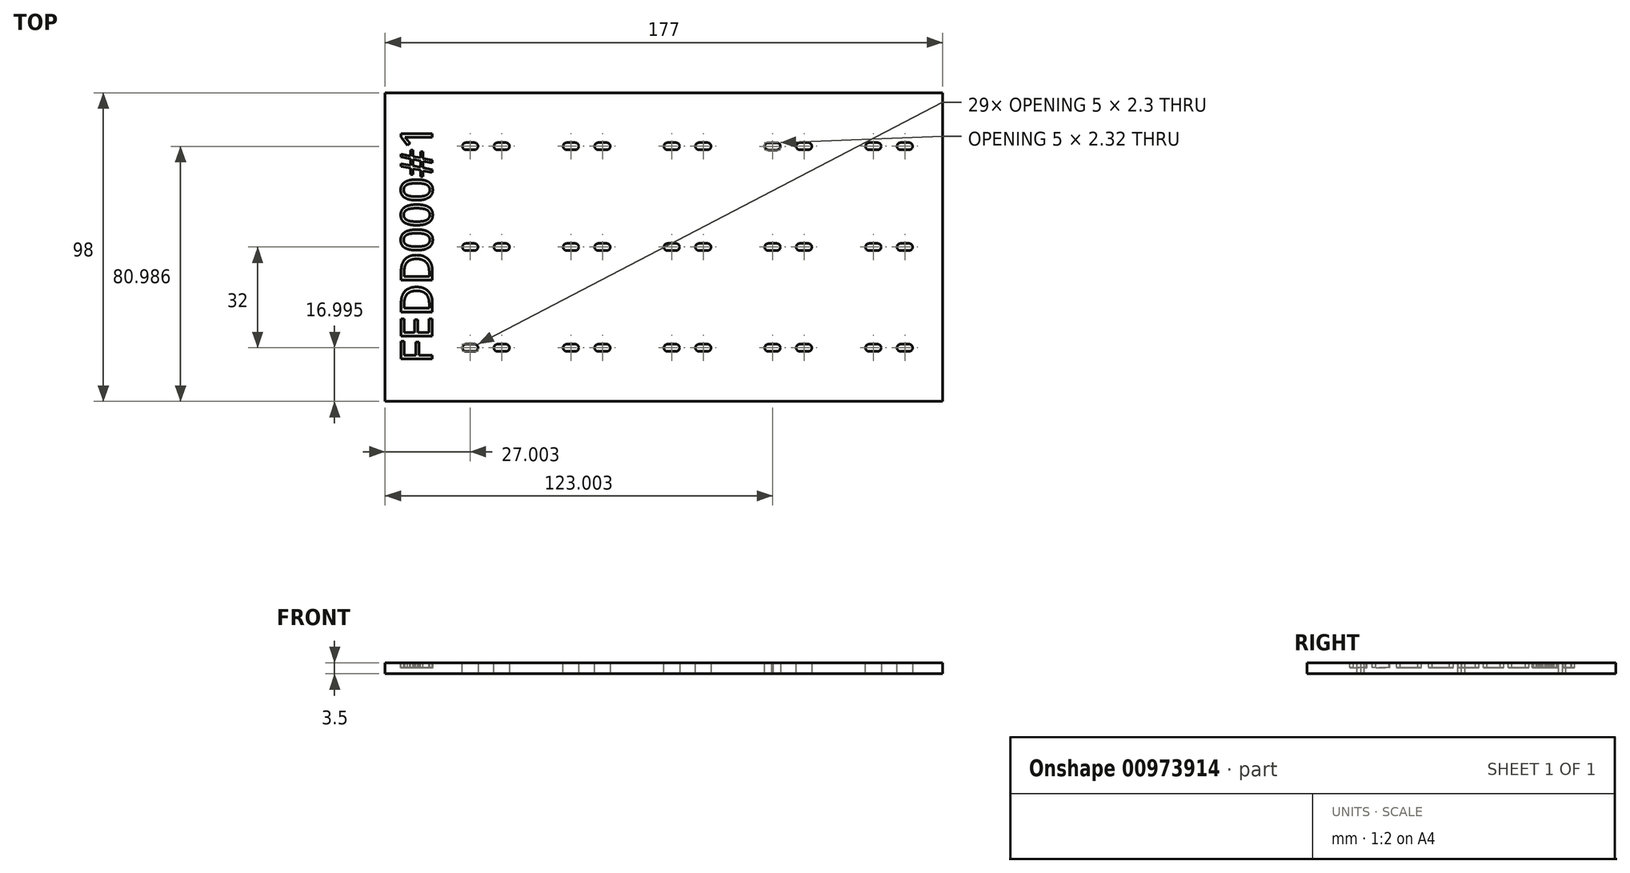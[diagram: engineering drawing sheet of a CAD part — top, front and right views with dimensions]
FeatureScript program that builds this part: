
annotation { "Feature Type Name" : "Feature", "Feature Type Description" : "" }
export const myFeature = defineFeature(function(context is Context, id is Id, definition is map)
    precondition{}
    {
        {
            var Q0;
            Q0=qCreatedBy(makeId("Top.planeOp"),FACE);
            var sketch = newSketch(context, id + "F0", { "sketchPlane" : qUnion([Q0])});
            skLineSegment(sketch, "E0.bottom", {"start": v(-87.55, 48.72) * mm, "end": v(89.45, 48.72) * mm});
            skLineSegment(sketch, "E0.top", {"start": v(-87.55, -49.28) * mm, "end": v(89.45, -49.28) * mm});
            skLineSegment(sketch, "E0.left", {"start": v(-87.55, 48.72) * mm, "end": v(-87.55, -49.28) * mm});
            skLineSegment(sketch, "E0.right", {"start": v(89.45, 48.72) * mm, "end": v(89.45, -49.28) * mm});
            skSolve(sketch);
        }
        {
            var Q0;
            Q0=makeQuery(id+"F0.imprint","IMPRINT",FACE,{"disambiguationData":[TD([[makeQuery(id+"F0.imprint","IMPRINT",EDGE,{"derivedFrom":sQuery(id+"F0.wireOp",EDGE,"E0.bottom")}),-1.0]])]});
            extrude(context, id + "F1", {"entities" : qUnion([Q0]), "depth" : 3.5 * mm, "offsetDistance" : 25 * mm});
        }
        {
            var Q0;
            Q0=makeQuery(id+"F1.opExtrude","CAP_FACE",FACE,{"disambiguationData":[OSD([sQuery(id+"F0.wireOp",EDGE,"E0.bottom"),sQuery(id+"F0.wireOp",EDGE,"E0.top"),sQuery(id+"F0.wireOp",EDGE,"E0.left"),sQuery(id+"F0.wireOp",EDGE,"E0.right")])],"isStart":false});
            var sketch = newSketch(context, id + "F2", { "sketchPlane" : qUnion([Q0])});
            skText(sketch, "E1", { "text": "FEDD000#1", "fontName": "OpenSans-Regular.ttf"});
            const initialGuessF2  = {"E1": [-0.07255, -0.03713, 0, 1, 0.01]};
            skSetInitialGuess(sketch, initialGuessF2);
            skSolve(sketch);
        }
        {
            var Q0;
            Q0=qSketchRegion(id+"F2",true);
            extrude(context, id + "F3", {"entities" : qUnion([Q0]), "operationType" : NewBodyOperationType.REMOVE, "oppositeDirection" : true, "depth" : 1.5 * mm, "offsetDistance" : 25 * mm});
        }
        {
            var Q0;
            {var subQ0=sQuery(id+"F0.wireOp",EDGE,"E0.left");var subQ1=sQuery(id+"F0.wireOp",EDGE,"E0.bottom");var subQ2=sQuery(id+"F0.wireOp",EDGE,"E0.right");var subQ3=sQuery(id+"F0.wireOp",EDGE,"E0.top");Q0=makeQuery(id+"F3.boolean.opBoolean","SPLIT",FACE,{"disambiguationData":[TD([makeQuery(id+"F1.opExtrude","SWEPT_FACE",FACE,{"disambiguationData":[OSD([subQ1])]})])],"derivedFrom":makeQuery(id+"F1.opExtrude","CAP_FACE",FACE,{"disambiguationData":[OSD([subQ1,subQ3,subQ0,subQ2])],"isStart":false})});}
            var sketch = newSketch(context, id + "F4", { "sketchPlane" : qUnion([Q0])});
            skCircle(sketch, "E2", {"center": v(-60.55, 31.72) * mm, "radius": 1.15 * mm});
            skCircle(sketch, "E3", {"center": v(-50.55, 31.72) * mm, "radius": 1.15 * mm});
            skCircle(sketch, "E4", {"center": v(-28.55, 31.72) * mm, "radius": 1.15 * mm});
            skCircle(sketch, "E5", {"center": v(-18.55, 31.72) * mm, "radius": 1.15 * mm});
            skCircle(sketch, "E6", {"center": v(3.45, 31.72) * mm, "radius": 1.15 * mm});
            skCircle(sketch, "E7", {"center": v(13.45, 31.72) * mm, "radius": 1.15 * mm});
            skCircle(sketch, "E8", {"center": v(35.45, 31.72) * mm, "radius": 1.15 * mm});
            skCircle(sketch, "E9", {"center": v(45.45, 31.72) * mm, "radius": 1.15 * mm});
            skCircle(sketch, "E10", {"center": v(67.45, 31.72) * mm, "radius": 1.15 * mm});
            skCircle(sketch, "E11", {"center": v(77.45, 31.72) * mm, "radius": 1.15 * mm});
            skCircle(sketch, "E12", {"center": v(-60.55, -0.28) * mm, "radius": 1.15 * mm});
            skCircle(sketch, "E13", {"center": v(-50.55, -0.28) * mm, "radius": 1.15 * mm});
            skCircle(sketch, "E14", {"center": v(-28.55, -0.28) * mm, "radius": 1.15 * mm});
            skCircle(sketch, "E15", {"center": v(-18.55, -0.28) * mm, "radius": 1.15 * mm});
            skCircle(sketch, "E16", {"center": v(3.45, -0.28) * mm, "radius": 1.15 * mm});
            skCircle(sketch, "E17", {"center": v(13.45, -0.28) * mm, "radius": 1.15 * mm});
            skCircle(sketch, "E18", {"center": v(35.45, -0.28) * mm, "radius": 1.15 * mm});
            skCircle(sketch, "E19", {"center": v(45.45, -0.28) * mm, "radius": 1.15 * mm});
            skCircle(sketch, "E20", {"center": v(67.45, -0.28) * mm, "radius": 1.15 * mm});
            skCircle(sketch, "E21", {"center": v(77.45, -0.28) * mm, "radius": 1.15 * mm});
            skCircle(sketch, "E22", {"center": v(-60.55, -32.28) * mm, "radius": 1.15 * mm});
            skCircle(sketch, "E23", {"center": v(-50.55, -32.28) * mm, "radius": 1.15 * mm});
            skCircle(sketch, "E24", {"center": v(-28.55, -32.28) * mm, "radius": 1.15 * mm});
            skCircle(sketch, "E25", {"center": v(-18.55, -32.28) * mm, "radius": 1.15 * mm});
            skCircle(sketch, "E26", {"center": v(3.45, -32.28) * mm, "radius": 1.15 * mm});
            skCircle(sketch, "E27", {"center": v(13.45, -32.28) * mm, "radius": 1.15 * mm});
            skCircle(sketch, "E28", {"center": v(35.45, -32.28) * mm, "radius": 1.15 * mm});
            skCircle(sketch, "E29", {"center": v(45.45, -32.28) * mm, "radius": 1.15 * mm});
            skCircle(sketch, "E30", {"center": v(67.45, -32.28) * mm, "radius": 1.15 * mm});
            skCircle(sketch, "E31", {"center": v(77.45, -32.28) * mm, "radius": 1.15 * mm});
            skLineSegment(sketch, "E32.bottom", {"start": v(-53.05, 32.87) * mm, "end": v(-48.05, 32.87) * mm});
            skLineSegment(sketch, "E32.top", {"start": v(-53.05, 30.57) * mm, "end": v(-48.05, 30.57) * mm});
            skLineSegment(sketch, "E32.left", {"start": v(-53.05, 32.87) * mm, "end": v(-53.05, 30.57) * mm});
            skLineSegment(sketch, "E32.right", {"start": v(-48.05, 32.87) * mm, "end": v(-48.05, 30.57) * mm});
            skLineSegment(sketch, "E33.bottom", {"start": v(-63.05, 32.87) * mm, "end": v(-58.05, 32.87) * mm});
            skLineSegment(sketch, "E33.top", {"start": v(-63.05, 30.57) * mm, "end": v(-58.05, 30.57) * mm});
            skLineSegment(sketch, "E33.left", {"start": v(-63.05, 32.87) * mm, "end": v(-63.05, 30.57) * mm});
            skLineSegment(sketch, "E33.right", {"start": v(-58.05, 32.87) * mm, "end": v(-58.05, 30.57) * mm});
            skLineSegment(sketch, "E34.bottom", {"start": v(-31.05, 32.87) * mm, "end": v(-26.05, 32.87) * mm});
            skLineSegment(sketch, "E34.top", {"start": v(-31.05, 30.57) * mm, "end": v(-26.05, 30.57) * mm});
            skLineSegment(sketch, "E34.left", {"start": v(-31.05, 32.87) * mm, "end": v(-31.05, 30.57) * mm});
            skLineSegment(sketch, "E34.right", {"start": v(-26.05, 32.87) * mm, "end": v(-26.05, 30.57) * mm});
            skLineSegment(sketch, "E35.bottom", {"start": v(-21.05, 32.87) * mm, "end": v(-16.05, 32.87) * mm});
            skLineSegment(sketch, "E35.top", {"start": v(-21.05, 30.57) * mm, "end": v(-16.05, 30.57) * mm});
            skLineSegment(sketch, "E35.left", {"start": v(-21.05, 32.87) * mm, "end": v(-21.05, 30.57) * mm});
            skLineSegment(sketch, "E35.right", {"start": v(-16.05, 32.87) * mm, "end": v(-16.05, 30.57) * mm});
            skLineSegment(sketch, "E36.bottom", {"start": v(0.95, 32.87) * mm, "end": v(5.95, 32.87) * mm});
            skLineSegment(sketch, "E36.top", {"start": v(0.95, 30.57) * mm, "end": v(5.95, 30.57) * mm});
            skLineSegment(sketch, "E36.left", {"start": v(0.95, 32.87) * mm, "end": v(0.95, 30.57) * mm});
            skLineSegment(sketch, "E36.right", {"start": v(5.95, 32.87) * mm, "end": v(5.95, 30.57) * mm});
            skLineSegment(sketch, "E37.bottom", {"start": v(10.95, 32.87) * mm, "end": v(15.95, 32.87) * mm});
            skLineSegment(sketch, "E37.top", {"start": v(10.95, 30.57) * mm, "end": v(15.95, 30.57) * mm});
            skLineSegment(sketch, "E37.left", {"start": v(10.95, 32.87) * mm, "end": v(10.95, 30.57) * mm});
            skLineSegment(sketch, "E37.right", {"start": v(15.95, 32.87) * mm, "end": v(15.95, 30.57) * mm});
            skLineSegment(sketch, "E38.bottom", {"start": v(32.95, 32.85) * mm, "end": v(37.95, 32.85) * mm});
            skLineSegment(sketch, "E38.top", {"start": v(32.95, 30.55) * mm, "end": v(37.95, 30.55) * mm});
            skLineSegment(sketch, "E38.left", {"start": v(32.95, 32.85) * mm, "end": v(32.95, 30.55) * mm});
            skLineSegment(sketch, "E38.right", {"start": v(37.95, 32.85) * mm, "end": v(37.95, 30.55) * mm});
            skLineSegment(sketch, "E39.bottom", {"start": v(42.95, 32.87) * mm, "end": v(47.95, 32.87) * mm});
            skLineSegment(sketch, "E39.top", {"start": v(42.95, 30.57) * mm, "end": v(47.95, 30.57) * mm});
            skLineSegment(sketch, "E39.left", {"start": v(42.95, 32.87) * mm, "end": v(42.95, 30.57) * mm});
            skLineSegment(sketch, "E39.right", {"start": v(47.95, 32.87) * mm, "end": v(47.95, 30.57) * mm});
            skLineSegment(sketch, "E40.bottom", {"start": v(64.95, 32.87) * mm, "end": v(69.95, 32.87) * mm});
            skLineSegment(sketch, "E40.top", {"start": v(64.95, 30.57) * mm, "end": v(69.95, 30.57) * mm});
            skLineSegment(sketch, "E40.left", {"start": v(64.95, 32.87) * mm, "end": v(64.95, 30.57) * mm});
            skLineSegment(sketch, "E40.right", {"start": v(69.95, 32.87) * mm, "end": v(69.95, 30.57) * mm});
            skLineSegment(sketch, "E41.bottom", {"start": v(74.95, 32.87) * mm, "end": v(79.95, 32.87) * mm});
            skLineSegment(sketch, "E41.top", {"start": v(74.95, 30.57) * mm, "end": v(79.95, 30.57) * mm});
            skLineSegment(sketch, "E41.left", {"start": v(74.95, 32.87) * mm, "end": v(74.95, 30.57) * mm});
            skLineSegment(sketch, "E41.right", {"start": v(79.95, 32.87) * mm, "end": v(79.95, 30.57) * mm});
            skLineSegment(sketch, "E42.bottom", {"start": v(74.95, 0.87) * mm, "end": v(79.95, 0.87) * mm});
            skLineSegment(sketch, "E42.top", {"start": v(74.95, -1.43) * mm, "end": v(79.95, -1.43) * mm});
            skLineSegment(sketch, "E42.left", {"start": v(74.95, 0.87) * mm, "end": v(74.95, -1.43) * mm});
            skLineSegment(sketch, "E42.right", {"start": v(79.95, 0.87) * mm, "end": v(79.95, -1.43) * mm});
            skLineSegment(sketch, "E43.bottom", {"start": v(64.95, 0.87) * mm, "end": v(69.95, 0.87) * mm});
            skLineSegment(sketch, "E43.top", {"start": v(64.95, -1.43) * mm, "end": v(69.95, -1.43) * mm});
            skLineSegment(sketch, "E43.left", {"start": v(64.95, 0.87) * mm, "end": v(64.95, -1.43) * mm});
            skLineSegment(sketch, "E43.right", {"start": v(69.95, 0.87) * mm, "end": v(69.95, -1.43) * mm});
            skLineSegment(sketch, "E44.bottom", {"start": v(42.95, 0.87) * mm, "end": v(47.95, 0.87) * mm});
            skLineSegment(sketch, "E44.top", {"start": v(42.95, -1.43) * mm, "end": v(47.95, -1.43) * mm});
            skLineSegment(sketch, "E44.left", {"start": v(42.95, 0.87) * mm, "end": v(42.95, -1.43) * mm});
            skLineSegment(sketch, "E44.right", {"start": v(47.95, 0.87) * mm, "end": v(47.95, -1.43) * mm});
            skLineSegment(sketch, "E45.bottom", {"start": v(32.95, 0.87) * mm, "end": v(37.95, 0.87) * mm});
            skLineSegment(sketch, "E45.top", {"start": v(32.95, -1.43) * mm, "end": v(37.95, -1.43) * mm});
            skLineSegment(sketch, "E45.left", {"start": v(32.95, 0.87) * mm, "end": v(32.95, -1.43) * mm});
            skLineSegment(sketch, "E45.right", {"start": v(37.95, 0.87) * mm, "end": v(37.95, -1.43) * mm});
            skLineSegment(sketch, "E46.bottom", {"start": v(10.95, 0.87) * mm, "end": v(15.95, 0.87) * mm});
            skLineSegment(sketch, "E46.top", {"start": v(10.95, -1.43) * mm, "end": v(15.95, -1.43) * mm});
            skLineSegment(sketch, "E46.left", {"start": v(10.95, 0.87) * mm, "end": v(10.95, -1.43) * mm});
            skLineSegment(sketch, "E46.right", {"start": v(15.95, 0.87) * mm, "end": v(15.95, -1.43) * mm});
            skLineSegment(sketch, "E47.bottom", {"start": v(-63.05, 0.87) * mm, "end": v(-58.05, 0.87) * mm});
            skLineSegment(sketch, "E47.top", {"start": v(-63.05, -1.43) * mm, "end": v(-58.05, -1.43) * mm});
            skLineSegment(sketch, "E47.left", {"start": v(-63.05, 0.87) * mm, "end": v(-63.05, -1.43) * mm});
            skLineSegment(sketch, "E47.right", {"start": v(-58.05, 0.87) * mm, "end": v(-58.05, -1.43) * mm});
            skLineSegment(sketch, "E48.bottom", {"start": v(-53.05, 0.87) * mm, "end": v(-48.05, 0.87) * mm});
            skLineSegment(sketch, "E48.top", {"start": v(-53.05, -1.43) * mm, "end": v(-48.05, -1.43) * mm});
            skLineSegment(sketch, "E48.left", {"start": v(-53.05, 0.87) * mm, "end": v(-53.05, -1.43) * mm});
            skLineSegment(sketch, "E48.right", {"start": v(-48.05, 0.87) * mm, "end": v(-48.05, -1.43) * mm});
            skLineSegment(sketch, "E49.bottom", {"start": v(-31.05, 0.87) * mm, "end": v(-26.05, 0.87) * mm});
            skLineSegment(sketch, "E49.top", {"start": v(-31.05, -1.43) * mm, "end": v(-26.05, -1.43) * mm});
            skLineSegment(sketch, "E49.left", {"start": v(-31.05, 0.87) * mm, "end": v(-31.05, -1.43) * mm});
            skLineSegment(sketch, "E49.right", {"start": v(-26.05, 0.87) * mm, "end": v(-26.05, -1.43) * mm});
            skLineSegment(sketch, "E50.bottom", {"start": v(-21.05, 0.87) * mm, "end": v(-16.05, 0.87) * mm});
            skLineSegment(sketch, "E50.top", {"start": v(-21.05, -1.43) * mm, "end": v(-16.05, -1.43) * mm});
            skLineSegment(sketch, "E50.left", {"start": v(-21.05, 0.87) * mm, "end": v(-21.05, -1.43) * mm});
            skLineSegment(sketch, "E50.right", {"start": v(-16.05, 0.87) * mm, "end": v(-16.05, -1.43) * mm});
            skLineSegment(sketch, "E51.bottom", {"start": v(0.95, 0.87) * mm, "end": v(5.95, 0.87) * mm});
            skLineSegment(sketch, "E51.top", {"start": v(0.95, -1.43) * mm, "end": v(5.95, -1.43) * mm});
            skLineSegment(sketch, "E51.left", {"start": v(0.95, 0.87) * mm, "end": v(0.95, -1.43) * mm});
            skLineSegment(sketch, "E51.right", {"start": v(5.95, 0.87) * mm, "end": v(5.95, -1.43) * mm});
            skLineSegment(sketch, "E52.bottom", {"start": v(-63.05, -31.13) * mm, "end": v(-58.05, -31.13) * mm});
            skLineSegment(sketch, "E52.top", {"start": v(-63.05, -33.43) * mm, "end": v(-58.05, -33.43) * mm});
            skLineSegment(sketch, "E52.left", {"start": v(-63.05, -31.13) * mm, "end": v(-63.05, -33.43) * mm});
            skLineSegment(sketch, "E52.right", {"start": v(-58.05, -31.13) * mm, "end": v(-58.05, -33.43) * mm});
            skLineSegment(sketch, "E53.bottom", {"start": v(-53.05, -31.13) * mm, "end": v(-48.05, -31.13) * mm});
            skLineSegment(sketch, "E53.top", {"start": v(-53.05, -33.43) * mm, "end": v(-48.05, -33.43) * mm});
            skLineSegment(sketch, "E53.left", {"start": v(-53.05, -31.13) * mm, "end": v(-53.05, -33.43) * mm});
            skLineSegment(sketch, "E53.right", {"start": v(-48.05, -31.13) * mm, "end": v(-48.05, -33.43) * mm});
            skLineSegment(sketch, "E54.bottom", {"start": v(-31.05, -31.13) * mm, "end": v(-26.05, -31.13) * mm});
            skLineSegment(sketch, "E54.top", {"start": v(-31.05, -33.43) * mm, "end": v(-26.05, -33.43) * mm});
            skLineSegment(sketch, "E54.left", {"start": v(-31.05, -31.13) * mm, "end": v(-31.05, -33.43) * mm});
            skLineSegment(sketch, "E54.right", {"start": v(-26.05, -31.13) * mm, "end": v(-26.05, -33.43) * mm});
            skLineSegment(sketch, "E55.bottom", {"start": v(-21.05, -31.13) * mm, "end": v(-16.05, -31.13) * mm});
            skLineSegment(sketch, "E55.top", {"start": v(-21.05, -33.43) * mm, "end": v(-16.05, -33.43) * mm});
            skLineSegment(sketch, "E55.left", {"start": v(-21.05, -31.13) * mm, "end": v(-21.05, -33.43) * mm});
            skLineSegment(sketch, "E55.right", {"start": v(-16.05, -31.13) * mm, "end": v(-16.05, -33.43) * mm});
            skLineSegment(sketch, "E56.bottom", {"start": v(0.95, -31.13) * mm, "end": v(5.95, -31.13) * mm});
            skLineSegment(sketch, "E56.top", {"start": v(0.95, -33.43) * mm, "end": v(5.95, -33.43) * mm});
            skLineSegment(sketch, "E56.left", {"start": v(0.95, -31.13) * mm, "end": v(0.95, -33.43) * mm});
            skLineSegment(sketch, "E56.right", {"start": v(5.95, -31.13) * mm, "end": v(5.95, -33.43) * mm});
            skLineSegment(sketch, "E57.bottom", {"start": v(10.95, -31.13) * mm, "end": v(15.95, -31.13) * mm});
            skLineSegment(sketch, "E57.top", {"start": v(10.95, -33.43) * mm, "end": v(15.95, -33.43) * mm});
            skLineSegment(sketch, "E57.left", {"start": v(10.95, -31.13) * mm, "end": v(10.95, -33.43) * mm});
            skLineSegment(sketch, "E57.right", {"start": v(15.95, -31.13) * mm, "end": v(15.95, -33.43) * mm});
            skLineSegment(sketch, "E58.bottom", {"start": v(32.95, -31.13) * mm, "end": v(37.95, -31.13) * mm});
            skLineSegment(sketch, "E58.top", {"start": v(32.95, -33.43) * mm, "end": v(37.95, -33.43) * mm});
            skLineSegment(sketch, "E58.left", {"start": v(32.95, -31.13) * mm, "end": v(32.95, -33.43) * mm});
            skLineSegment(sketch, "E58.right", {"start": v(37.95, -31.13) * mm, "end": v(37.95, -33.43) * mm});
            skLineSegment(sketch, "E59.bottom", {"start": v(42.95, -31.13) * mm, "end": v(47.95, -31.13) * mm});
            skLineSegment(sketch, "E59.top", {"start": v(42.95, -33.43) * mm, "end": v(47.95, -33.43) * mm});
            skLineSegment(sketch, "E59.left", {"start": v(42.95, -31.13) * mm, "end": v(42.95, -33.43) * mm});
            skLineSegment(sketch, "E59.right", {"start": v(47.95, -31.13) * mm, "end": v(47.95, -33.43) * mm});
            skLineSegment(sketch, "E60.bottom", {"start": v(64.95, -31.13) * mm, "end": v(69.95, -31.13) * mm});
            skLineSegment(sketch, "E60.top", {"start": v(64.95, -33.43) * mm, "end": v(69.95, -33.43) * mm});
            skLineSegment(sketch, "E60.left", {"start": v(64.95, -31.13) * mm, "end": v(64.95, -33.43) * mm});
            skLineSegment(sketch, "E60.right", {"start": v(69.95, -31.13) * mm, "end": v(69.95, -33.43) * mm});
            skLineSegment(sketch, "E61.bottom", {"start": v(74.95, -31.13) * mm, "end": v(79.95, -31.13) * mm});
            skLineSegment(sketch, "E61.top", {"start": v(74.95, -33.43) * mm, "end": v(79.95, -33.43) * mm});
            skLineSegment(sketch, "E61.left", {"start": v(74.95, -31.13) * mm, "end": v(74.95, -33.43) * mm});
            skLineSegment(sketch, "E61.right", {"start": v(79.95, -31.13) * mm, "end": v(79.95, -33.43) * mm});
            skSolve(sketch);
        }
        {
            var Q0;
            Q0=qSketchRegion(id+"F4",true);
            extrude(context, id + "F5", {"entities" : qUnion([Q0]), "operationType" : NewBodyOperationType.REMOVE, "endBound" : BoundingType.UP_TO_NEXT, "oppositeDirection" : true, "depth" : 25 * mm, "offsetDistance" : 25 * mm});
        }
        {
            var Q0;
            Q0=makeQuery(id+"F5.boolean.opBoolean","COPY",EDGE,{"derivedFrom":makeQuery(id+"F5.opExtrude","SWEPT_EDGE",EDGE,{"disambiguationData":[OSD([sQuery(id+"F4.wireOp",EDGE,"E32.bottom"),sQuery(id+"F4.wireOp",EDGE,"E32.left")])]})});
            var Q1;
            Q1=makeQuery(id+"F5.boolean.opBoolean","COPY",EDGE,{"derivedFrom":makeQuery(id+"F5.opExtrude","SWEPT_EDGE",EDGE,{"disambiguationData":[OSD([sQuery(id+"F4.wireOp",EDGE,"E32.bottom"),sQuery(id+"F4.wireOp",EDGE,"E32.right")])]})});
            var Q2;
            Q2=makeQuery(id+"F5.boolean.opBoolean","COPY",EDGE,{"derivedFrom":makeQuery(id+"F5.opExtrude","SWEPT_EDGE",EDGE,{"disambiguationData":[OSD([sQuery(id+"F4.wireOp",EDGE,"E32.top"),sQuery(id+"F4.wireOp",EDGE,"E32.right")])]})});
            var Q3;
            Q3=makeQuery(id+"F5.boolean.opBoolean","COPY",EDGE,{"derivedFrom":makeQuery(id+"F5.opExtrude","SWEPT_EDGE",EDGE,{"disambiguationData":[OSD([sQuery(id+"F4.wireOp",EDGE,"E32.top"),sQuery(id+"F4.wireOp",EDGE,"E32.left")])]})});
            var Q4;
            Q4=makeQuery(id+"F5.boolean.opBoolean","COPY",EDGE,{"derivedFrom":makeQuery(id+"F5.opExtrude","SWEPT_EDGE",EDGE,{"disambiguationData":[OSD([sQuery(id+"F4.wireOp",EDGE,"E33.bottom"),sQuery(id+"F4.wireOp",EDGE,"E33.left")])]})});
            var Q5;
            Q5=makeQuery(id+"F5.boolean.opBoolean","COPY",EDGE,{"derivedFrom":makeQuery(id+"F5.opExtrude","SWEPT_EDGE",EDGE,{"disambiguationData":[OSD([sQuery(id+"F4.wireOp",EDGE,"E47.bottom"),sQuery(id+"F4.wireOp",EDGE,"E47.left")])]})});
            var Q6;
            Q6=makeQuery(id+"F5.boolean.opBoolean","COPY",EDGE,{"derivedFrom":makeQuery(id+"F5.opExtrude","SWEPT_EDGE",EDGE,{"disambiguationData":[OSD([sQuery(id+"F4.wireOp",EDGE,"E48.bottom"),sQuery(id+"F4.wireOp",EDGE,"E48.left")])]})});
            var Q7;
            Q7=makeQuery(id+"F5.boolean.opBoolean","COPY",EDGE,{"derivedFrom":makeQuery(id+"F5.opExtrude","SWEPT_EDGE",EDGE,{"disambiguationData":[OSD([sQuery(id+"F4.wireOp",EDGE,"E49.bottom"),sQuery(id+"F4.wireOp",EDGE,"E49.left")])]})});
            var Q8;
            Q8=makeQuery(id+"F5.boolean.opBoolean","COPY",EDGE,{"derivedFrom":makeQuery(id+"F5.opExtrude","SWEPT_EDGE",EDGE,{"disambiguationData":[OSD([sQuery(id+"F4.wireOp",EDGE,"E50.bottom"),sQuery(id+"F4.wireOp",EDGE,"E50.left")])]})});
            var Q9;
            Q9=makeQuery(id+"F5.boolean.opBoolean","COPY",EDGE,{"derivedFrom":makeQuery(id+"F5.opExtrude","SWEPT_EDGE",EDGE,{"disambiguationData":[OSD([sQuery(id+"F4.wireOp",EDGE,"E34.bottom"),sQuery(id+"F4.wireOp",EDGE,"E34.left")])]})});
            var Q10;
            Q10=makeQuery(id+"F5.boolean.opBoolean","COPY",EDGE,{"derivedFrom":makeQuery(id+"F5.opExtrude","SWEPT_EDGE",EDGE,{"disambiguationData":[OSD([sQuery(id+"F4.wireOp",EDGE,"E35.bottom"),sQuery(id+"F4.wireOp",EDGE,"E35.left")])]})});
            var Q11;
            Q11=makeQuery(id+"F5.boolean.opBoolean","COPY",EDGE,{"derivedFrom":makeQuery(id+"F5.opExtrude","SWEPT_EDGE",EDGE,{"disambiguationData":[OSD([sQuery(id+"F4.wireOp",EDGE,"E52.bottom"),sQuery(id+"F4.wireOp",EDGE,"E52.left")])]})});
            var Q12;
            Q12=makeQuery(id+"F5.boolean.opBoolean","COPY",EDGE,{"derivedFrom":makeQuery(id+"F5.opExtrude","SWEPT_EDGE",EDGE,{"disambiguationData":[OSD([sQuery(id+"F4.wireOp",EDGE,"E53.bottom"),sQuery(id+"F4.wireOp",EDGE,"E53.left")])]})});
            var Q13;
            Q13=makeQuery(id+"F5.boolean.opBoolean","COPY",EDGE,{"derivedFrom":makeQuery(id+"F5.opExtrude","SWEPT_EDGE",EDGE,{"disambiguationData":[OSD([sQuery(id+"F4.wireOp",EDGE,"E54.bottom"),sQuery(id+"F4.wireOp",EDGE,"E54.left")])]})});
            var Q14;
            Q14=makeQuery(id+"F5.boolean.opBoolean","COPY",EDGE,{"derivedFrom":makeQuery(id+"F5.opExtrude","SWEPT_EDGE",EDGE,{"disambiguationData":[OSD([sQuery(id+"F4.wireOp",EDGE,"E55.bottom"),sQuery(id+"F4.wireOp",EDGE,"E55.left")])]})});
            var Q15;
            Q15=makeQuery(id+"F5.boolean.opBoolean","COPY",EDGE,{"derivedFrom":makeQuery(id+"F5.opExtrude","SWEPT_EDGE",EDGE,{"disambiguationData":[OSD([sQuery(id+"F4.wireOp",EDGE,"E56.bottom"),sQuery(id+"F4.wireOp",EDGE,"E56.left")])]})});
            var Q16;
            Q16=makeQuery(id+"F5.boolean.opBoolean","COPY",EDGE,{"derivedFrom":makeQuery(id+"F5.opExtrude","SWEPT_EDGE",EDGE,{"disambiguationData":[OSD([sQuery(id+"F4.wireOp",EDGE,"E57.bottom"),sQuery(id+"F4.wireOp",EDGE,"E57.left")])]})});
            var Q17;
            Q17=makeQuery(id+"F5.boolean.opBoolean","COPY",EDGE,{"derivedFrom":makeQuery(id+"F5.opExtrude","SWEPT_EDGE",EDGE,{"disambiguationData":[OSD([sQuery(id+"F4.wireOp",EDGE,"E36.bottom"),sQuery(id+"F4.wireOp",EDGE,"E36.left")])]})});
            var Q18;
            Q18=makeQuery(id+"F5.boolean.opBoolean","COPY",EDGE,{"derivedFrom":makeQuery(id+"F5.opExtrude","SWEPT_EDGE",EDGE,{"disambiguationData":[OSD([sQuery(id+"F4.wireOp",EDGE,"E37.bottom"),sQuery(id+"F4.wireOp",EDGE,"E37.left")])]})});
            var Q19;
            Q19=makeQuery(id+"F5.boolean.opBoolean","COPY",EDGE,{"derivedFrom":makeQuery(id+"F5.opExtrude","SWEPT_EDGE",EDGE,{"disambiguationData":[OSD([sQuery(id+"F4.wireOp",EDGE,"E38.bottom"),sQuery(id+"F4.wireOp",EDGE,"E38.left")])]})});
            var Q20;
            Q20=makeQuery(id+"F5.boolean.opBoolean","COPY",EDGE,{"derivedFrom":makeQuery(id+"F5.opExtrude","SWEPT_EDGE",EDGE,{"disambiguationData":[OSD([sQuery(id+"F4.wireOp",EDGE,"E39.bottom"),sQuery(id+"F4.wireOp",EDGE,"E39.left")])]})});
            var Q21;
            Q21=makeQuery(id+"F5.boolean.opBoolean","COPY",EDGE,{"derivedFrom":makeQuery(id+"F5.opExtrude","SWEPT_EDGE",EDGE,{"disambiguationData":[OSD([sQuery(id+"F4.wireOp",EDGE,"E40.bottom"),sQuery(id+"F4.wireOp",EDGE,"E40.left")])]})});
            var Q22;
            Q22=makeQuery(id+"F5.boolean.opBoolean","COPY",EDGE,{"derivedFrom":makeQuery(id+"F5.opExtrude","SWEPT_EDGE",EDGE,{"disambiguationData":[OSD([sQuery(id+"F4.wireOp",EDGE,"E41.bottom"),sQuery(id+"F4.wireOp",EDGE,"E41.left")])]})});
            var Q23;
            Q23=makeQuery(id+"F5.boolean.opBoolean","COPY",EDGE,{"derivedFrom":makeQuery(id+"F5.opExtrude","SWEPT_EDGE",EDGE,{"disambiguationData":[OSD([sQuery(id+"F4.wireOp",EDGE,"E60.bottom"),sQuery(id+"F4.wireOp",EDGE,"E60.left")])]})});
            var Q24;
            Q24=makeQuery(id+"F5.boolean.opBoolean","COPY",EDGE,{"derivedFrom":makeQuery(id+"F5.opExtrude","SWEPT_EDGE",EDGE,{"disambiguationData":[OSD([sQuery(id+"F4.wireOp",EDGE,"E59.bottom"),sQuery(id+"F4.wireOp",EDGE,"E59.left")])]})});
            var Q25;
            Q25=makeQuery(id+"F5.boolean.opBoolean","COPY",EDGE,{"derivedFrom":makeQuery(id+"F5.opExtrude","SWEPT_EDGE",EDGE,{"disambiguationData":[OSD([sQuery(id+"F4.wireOp",EDGE,"E58.bottom"),sQuery(id+"F4.wireOp",EDGE,"E58.left")])]})});
            var Q26;
            Q26=makeQuery(id+"F5.boolean.opBoolean","COPY",EDGE,{"derivedFrom":makeQuery(id+"F5.opExtrude","SWEPT_EDGE",EDGE,{"disambiguationData":[OSD([sQuery(id+"F4.wireOp",EDGE,"E51.bottom"),sQuery(id+"F4.wireOp",EDGE,"E51.left")])]})});
            var Q27;
            Q27=makeQuery(id+"F5.boolean.opBoolean","COPY",EDGE,{"derivedFrom":makeQuery(id+"F5.opExtrude","SWEPT_EDGE",EDGE,{"disambiguationData":[OSD([sQuery(id+"F4.wireOp",EDGE,"E46.bottom"),sQuery(id+"F4.wireOp",EDGE,"E46.left")])]})});
            var Q28;
            Q28=makeQuery(id+"F5.boolean.opBoolean","COPY",EDGE,{"derivedFrom":makeQuery(id+"F5.opExtrude","SWEPT_EDGE",EDGE,{"disambiguationData":[OSD([sQuery(id+"F4.wireOp",EDGE,"E45.bottom"),sQuery(id+"F4.wireOp",EDGE,"E45.left")])]})});
            var Q29;
            Q29=makeQuery(id+"F5.boolean.opBoolean","COPY",EDGE,{"derivedFrom":makeQuery(id+"F5.opExtrude","SWEPT_EDGE",EDGE,{"disambiguationData":[OSD([sQuery(id+"F4.wireOp",EDGE,"E44.bottom"),sQuery(id+"F4.wireOp",EDGE,"E44.left")])]})});
            var Q30;
            Q30=makeQuery(id+"F5.boolean.opBoolean","COPY",EDGE,{"derivedFrom":makeQuery(id+"F5.opExtrude","SWEPT_EDGE",EDGE,{"disambiguationData":[OSD([sQuery(id+"F4.wireOp",EDGE,"E43.bottom"),sQuery(id+"F4.wireOp",EDGE,"E43.left")])]})});
            var Q31;
            Q31=makeQuery(id+"F5.boolean.opBoolean","COPY",EDGE,{"derivedFrom":makeQuery(id+"F5.opExtrude","SWEPT_EDGE",EDGE,{"disambiguationData":[OSD([sQuery(id+"F4.wireOp",EDGE,"E42.bottom"),sQuery(id+"F4.wireOp",EDGE,"E42.left")])]})});
            var Q32;
            Q32=makeQuery(id+"F5.boolean.opBoolean","COPY",EDGE,{"derivedFrom":makeQuery(id+"F5.opExtrude","SWEPT_EDGE",EDGE,{"disambiguationData":[OSD([sQuery(id+"F4.wireOp",EDGE,"E61.bottom"),sQuery(id+"F4.wireOp",EDGE,"E61.left")])]})});
            var Q33;
            Q33=makeQuery(id+"F5.boolean.opBoolean","COPY",EDGE,{"derivedFrom":makeQuery(id+"F5.opExtrude","SWEPT_EDGE",EDGE,{"disambiguationData":[OSD([sQuery(id+"F4.wireOp",EDGE,"E33.bottom"),sQuery(id+"F4.wireOp",EDGE,"E33.right")])]})});
            var Q34;
            Q34=makeQuery(id+"F5.boolean.opBoolean","COPY",EDGE,{"derivedFrom":makeQuery(id+"F5.opExtrude","SWEPT_EDGE",EDGE,{"disambiguationData":[OSD([sQuery(id+"F4.wireOp",EDGE,"E34.bottom"),sQuery(id+"F4.wireOp",EDGE,"E34.right")])]})});
            var Q35;
            Q35=makeQuery(id+"F5.boolean.opBoolean","COPY",EDGE,{"derivedFrom":makeQuery(id+"F5.opExtrude","SWEPT_EDGE",EDGE,{"disambiguationData":[OSD([sQuery(id+"F4.wireOp",EDGE,"E35.bottom"),sQuery(id+"F4.wireOp",EDGE,"E35.right")])]})});
            var Q36;
            Q36=makeQuery(id+"F5.boolean.opBoolean","COPY",EDGE,{"derivedFrom":makeQuery(id+"F5.opExtrude","SWEPT_EDGE",EDGE,{"disambiguationData":[OSD([sQuery(id+"F4.wireOp",EDGE,"E50.bottom"),sQuery(id+"F4.wireOp",EDGE,"E50.right")])]})});
            var Q37;
            Q37=makeQuery(id+"F5.boolean.opBoolean","COPY",EDGE,{"derivedFrom":makeQuery(id+"F5.opExtrude","SWEPT_EDGE",EDGE,{"disambiguationData":[OSD([sQuery(id+"F4.wireOp",EDGE,"E48.bottom"),sQuery(id+"F4.wireOp",EDGE,"E48.right")])]})});
            var Q38;
            Q38=makeQuery(id+"F5.boolean.opBoolean","COPY",EDGE,{"derivedFrom":makeQuery(id+"F5.opExtrude","SWEPT_EDGE",EDGE,{"disambiguationData":[OSD([sQuery(id+"F4.wireOp",EDGE,"E47.bottom"),sQuery(id+"F4.wireOp",EDGE,"E47.right")])]})});
            var Q39;
            Q39=makeQuery(id+"F5.boolean.opBoolean","COPY",EDGE,{"derivedFrom":makeQuery(id+"F5.opExtrude","SWEPT_EDGE",EDGE,{"disambiguationData":[OSD([sQuery(id+"F4.wireOp",EDGE,"E52.bottom"),sQuery(id+"F4.wireOp",EDGE,"E52.right")])]})});
            var Q40;
            Q40=makeQuery(id+"F5.boolean.opBoolean","COPY",EDGE,{"derivedFrom":makeQuery(id+"F5.opExtrude","SWEPT_EDGE",EDGE,{"disambiguationData":[OSD([sQuery(id+"F4.wireOp",EDGE,"E53.bottom"),sQuery(id+"F4.wireOp",EDGE,"E53.right")])]})});
            var Q41;
            Q41=makeQuery(id+"F5.boolean.opBoolean","COPY",EDGE,{"derivedFrom":makeQuery(id+"F5.opExtrude","SWEPT_EDGE",EDGE,{"disambiguationData":[OSD([sQuery(id+"F4.wireOp",EDGE,"E54.bottom"),sQuery(id+"F4.wireOp",EDGE,"E54.right")])]})});
            var Q42;
            Q42=makeQuery(id+"F5.boolean.opBoolean","COPY",EDGE,{"derivedFrom":makeQuery(id+"F5.opExtrude","SWEPT_EDGE",EDGE,{"disambiguationData":[OSD([sQuery(id+"F4.wireOp",EDGE,"E55.bottom"),sQuery(id+"F4.wireOp",EDGE,"E55.right")])]})});
            var Q43;
            Q43=makeQuery(id+"F5.boolean.opBoolean","COPY",EDGE,{"derivedFrom":makeQuery(id+"F5.opExtrude","SWEPT_EDGE",EDGE,{"disambiguationData":[OSD([sQuery(id+"F4.wireOp",EDGE,"E51.bottom"),sQuery(id+"F4.wireOp",EDGE,"E51.right")])]})});
            var Q44;
            Q44=makeQuery(id+"F5.boolean.opBoolean","COPY",EDGE,{"derivedFrom":makeQuery(id+"F5.opExtrude","SWEPT_EDGE",EDGE,{"disambiguationData":[OSD([sQuery(id+"F4.wireOp",EDGE,"E46.bottom"),sQuery(id+"F4.wireOp",EDGE,"E46.right")])]})});
            var Q45;
            Q45=makeQuery(id+"F5.boolean.opBoolean","COPY",EDGE,{"derivedFrom":makeQuery(id+"F5.opExtrude","SWEPT_EDGE",EDGE,{"disambiguationData":[OSD([sQuery(id+"F4.wireOp",EDGE,"E36.bottom"),sQuery(id+"F4.wireOp",EDGE,"E36.right")])]})});
            var Q46;
            Q46=makeQuery(id+"F5.boolean.opBoolean","COPY",EDGE,{"derivedFrom":makeQuery(id+"F5.opExtrude","SWEPT_EDGE",EDGE,{"disambiguationData":[OSD([sQuery(id+"F4.wireOp",EDGE,"E37.bottom"),sQuery(id+"F4.wireOp",EDGE,"E37.right")])]})});
            var Q47;
            Q47=makeQuery(id+"F5.boolean.opBoolean","COPY",EDGE,{"derivedFrom":makeQuery(id+"F5.opExtrude","SWEPT_EDGE",EDGE,{"disambiguationData":[OSD([sQuery(id+"F4.wireOp",EDGE,"E38.bottom"),sQuery(id+"F4.wireOp",EDGE,"E38.right")])]})});
            var Q48;
            Q48=makeQuery(id+"F5.boolean.opBoolean","COPY",EDGE,{"derivedFrom":makeQuery(id+"F5.opExtrude","SWEPT_EDGE",EDGE,{"disambiguationData":[OSD([sQuery(id+"F4.wireOp",EDGE,"E39.bottom"),sQuery(id+"F4.wireOp",EDGE,"E39.right")])]})});
            var Q49;
            Q49=makeQuery(id+"F5.boolean.opBoolean","COPY",EDGE,{"derivedFrom":makeQuery(id+"F5.opExtrude","SWEPT_EDGE",EDGE,{"disambiguationData":[OSD([sQuery(id+"F4.wireOp",EDGE,"E56.bottom"),sQuery(id+"F4.wireOp",EDGE,"E56.right")])]})});
            var Q50;
            Q50=makeQuery(id+"F5.boolean.opBoolean","COPY",EDGE,{"derivedFrom":makeQuery(id+"F5.opExtrude","SWEPT_EDGE",EDGE,{"disambiguationData":[OSD([sQuery(id+"F4.wireOp",EDGE,"E57.bottom"),sQuery(id+"F4.wireOp",EDGE,"E57.right")])]})});
            var Q51;
            Q51=makeQuery(id+"F5.boolean.opBoolean","COPY",EDGE,{"derivedFrom":makeQuery(id+"F5.opExtrude","SWEPT_EDGE",EDGE,{"disambiguationData":[OSD([sQuery(id+"F4.wireOp",EDGE,"E58.bottom"),sQuery(id+"F4.wireOp",EDGE,"E58.right")])]})});
            var Q52;
            Q52=makeQuery(id+"F5.boolean.opBoolean","COPY",EDGE,{"derivedFrom":makeQuery(id+"F5.opExtrude","SWEPT_EDGE",EDGE,{"disambiguationData":[OSD([sQuery(id+"F4.wireOp",EDGE,"E59.bottom"),sQuery(id+"F4.wireOp",EDGE,"E59.right")])]})});
            var Q53;
            Q53=makeQuery(id+"F5.boolean.opBoolean","COPY",EDGE,{"derivedFrom":makeQuery(id+"F5.opExtrude","SWEPT_EDGE",EDGE,{"disambiguationData":[OSD([sQuery(id+"F4.wireOp",EDGE,"E60.bottom"),sQuery(id+"F4.wireOp",EDGE,"E60.right")])]})});
            var Q54;
            Q54=makeQuery(id+"F5.boolean.opBoolean","COPY",EDGE,{"derivedFrom":makeQuery(id+"F5.opExtrude","SWEPT_EDGE",EDGE,{"disambiguationData":[OSD([sQuery(id+"F4.wireOp",EDGE,"E61.bottom"),sQuery(id+"F4.wireOp",EDGE,"E61.right")])]})});
            var Q55;
            Q55=makeQuery(id+"F5.boolean.opBoolean","COPY",EDGE,{"derivedFrom":makeQuery(id+"F5.opExtrude","SWEPT_EDGE",EDGE,{"disambiguationData":[OSD([sQuery(id+"F4.wireOp",EDGE,"E45.bottom"),sQuery(id+"F4.wireOp",EDGE,"E45.right")])]})});
            var Q56;
            Q56=makeQuery(id+"F5.boolean.opBoolean","COPY",EDGE,{"derivedFrom":makeQuery(id+"F5.opExtrude","SWEPT_EDGE",EDGE,{"disambiguationData":[OSD([sQuery(id+"F4.wireOp",EDGE,"E44.bottom"),sQuery(id+"F4.wireOp",EDGE,"E44.right")])]})});
            var Q57;
            Q57=makeQuery(id+"F5.boolean.opBoolean","COPY",EDGE,{"derivedFrom":makeQuery(id+"F5.opExtrude","SWEPT_EDGE",EDGE,{"disambiguationData":[OSD([sQuery(id+"F4.wireOp",EDGE,"E43.bottom"),sQuery(id+"F4.wireOp",EDGE,"E43.right")])]})});
            var Q58;
            Q58=makeQuery(id+"F5.boolean.opBoolean","COPY",EDGE,{"derivedFrom":makeQuery(id+"F5.opExtrude","SWEPT_EDGE",EDGE,{"disambiguationData":[OSD([sQuery(id+"F4.wireOp",EDGE,"E42.bottom"),sQuery(id+"F4.wireOp",EDGE,"E42.right")])]})});
            var Q59;
            Q59=makeQuery(id+"F5.boolean.opBoolean","COPY",EDGE,{"derivedFrom":makeQuery(id+"F5.opExtrude","SWEPT_EDGE",EDGE,{"disambiguationData":[OSD([sQuery(id+"F4.wireOp",EDGE,"E41.bottom"),sQuery(id+"F4.wireOp",EDGE,"E41.right")])]})});
            var Q60;
            Q60=makeQuery(id+"F5.boolean.opBoolean","COPY",EDGE,{"derivedFrom":makeQuery(id+"F5.opExtrude","SWEPT_EDGE",EDGE,{"disambiguationData":[OSD([sQuery(id+"F4.wireOp",EDGE,"E40.bottom"),sQuery(id+"F4.wireOp",EDGE,"E40.right")])]})});
            var Q61;
            Q61=makeQuery(id+"F5.boolean.opBoolean","COPY",EDGE,{"derivedFrom":makeQuery(id+"F5.opExtrude","SWEPT_EDGE",EDGE,{"disambiguationData":[OSD([sQuery(id+"F4.wireOp",EDGE,"E61.top"),sQuery(id+"F4.wireOp",EDGE,"E61.left")])]})});
            var Q62;
            Q62=makeQuery(id+"F5.boolean.opBoolean","COPY",EDGE,{"derivedFrom":makeQuery(id+"F5.opExtrude","SWEPT_EDGE",EDGE,{"disambiguationData":[OSD([sQuery(id+"F4.wireOp",EDGE,"E60.top"),sQuery(id+"F4.wireOp",EDGE,"E60.left")])]})});
            var Q63;
            Q63=makeQuery(id+"F5.boolean.opBoolean","COPY",EDGE,{"derivedFrom":makeQuery(id+"F5.opExtrude","SWEPT_EDGE",EDGE,{"disambiguationData":[OSD([sQuery(id+"F4.wireOp",EDGE,"E59.top"),sQuery(id+"F4.wireOp",EDGE,"E59.left")])]})});
            var Q64;
            Q64=makeQuery(id+"F5.boolean.opBoolean","COPY",EDGE,{"derivedFrom":makeQuery(id+"F5.opExtrude","SWEPT_EDGE",EDGE,{"disambiguationData":[OSD([sQuery(id+"F4.wireOp",EDGE,"E58.top"),sQuery(id+"F4.wireOp",EDGE,"E58.left")])]})});
            var Q65;
            Q65=makeQuery(id+"F5.boolean.opBoolean","COPY",EDGE,{"derivedFrom":makeQuery(id+"F5.opExtrude","SWEPT_EDGE",EDGE,{"disambiguationData":[OSD([sQuery(id+"F4.wireOp",EDGE,"E57.top"),sQuery(id+"F4.wireOp",EDGE,"E57.left")])]})});
            var Q66;
            Q66=makeQuery(id+"F5.boolean.opBoolean","COPY",EDGE,{"derivedFrom":makeQuery(id+"F5.opExtrude","SWEPT_EDGE",EDGE,{"disambiguationData":[OSD([sQuery(id+"F4.wireOp",EDGE,"E56.top"),sQuery(id+"F4.wireOp",EDGE,"E56.left")])]})});
            var Q67;
            Q67=makeQuery(id+"F5.boolean.opBoolean","COPY",EDGE,{"derivedFrom":makeQuery(id+"F5.opExtrude","SWEPT_EDGE",EDGE,{"disambiguationData":[OSD([sQuery(id+"F4.wireOp",EDGE,"E55.top"),sQuery(id+"F4.wireOp",EDGE,"E55.left")])]})});
            var Q68;
            Q68=makeQuery(id+"F5.boolean.opBoolean","COPY",EDGE,{"derivedFrom":makeQuery(id+"F5.opExtrude","SWEPT_EDGE",EDGE,{"disambiguationData":[OSD([sQuery(id+"F4.wireOp",EDGE,"E54.top"),sQuery(id+"F4.wireOp",EDGE,"E54.left")])]})});
            var Q69;
            Q69=makeQuery(id+"F5.boolean.opBoolean","COPY",EDGE,{"derivedFrom":makeQuery(id+"F5.opExtrude","SWEPT_EDGE",EDGE,{"disambiguationData":[OSD([sQuery(id+"F4.wireOp",EDGE,"E42.top"),sQuery(id+"F4.wireOp",EDGE,"E42.left")])]})});
            var Q70;
            Q70=makeQuery(id+"F5.boolean.opBoolean","COPY",EDGE,{"derivedFrom":makeQuery(id+"F5.opExtrude","SWEPT_EDGE",EDGE,{"disambiguationData":[OSD([sQuery(id+"F4.wireOp",EDGE,"E43.top"),sQuery(id+"F4.wireOp",EDGE,"E43.left")])]})});
            var Q71;
            Q71=makeQuery(id+"F5.boolean.opBoolean","COPY",EDGE,{"derivedFrom":makeQuery(id+"F5.opExtrude","SWEPT_EDGE",EDGE,{"disambiguationData":[OSD([sQuery(id+"F4.wireOp",EDGE,"E44.top"),sQuery(id+"F4.wireOp",EDGE,"E44.left")])]})});
            var Q72;
            Q72=makeQuery(id+"F5.boolean.opBoolean","COPY",EDGE,{"derivedFrom":makeQuery(id+"F5.opExtrude","SWEPT_EDGE",EDGE,{"disambiguationData":[OSD([sQuery(id+"F4.wireOp",EDGE,"E45.top"),sQuery(id+"F4.wireOp",EDGE,"E45.left")])]})});
            var Q73;
            Q73=makeQuery(id+"F5.boolean.opBoolean","COPY",EDGE,{"derivedFrom":makeQuery(id+"F5.opExtrude","SWEPT_EDGE",EDGE,{"disambiguationData":[OSD([sQuery(id+"F4.wireOp",EDGE,"E46.top"),sQuery(id+"F4.wireOp",EDGE,"E46.left")])]})});
            var Q74;
            Q74=makeQuery(id+"F5.boolean.opBoolean","COPY",EDGE,{"derivedFrom":makeQuery(id+"F5.opExtrude","SWEPT_EDGE",EDGE,{"disambiguationData":[OSD([sQuery(id+"F4.wireOp",EDGE,"E51.top"),sQuery(id+"F4.wireOp",EDGE,"E51.left")])]})});
            var Q75;
            Q75=makeQuery(id+"F5.boolean.opBoolean","COPY",EDGE,{"derivedFrom":makeQuery(id+"F5.opExtrude","SWEPT_EDGE",EDGE,{"disambiguationData":[OSD([sQuery(id+"F4.wireOp",EDGE,"E50.top"),sQuery(id+"F4.wireOp",EDGE,"E50.left")])]})});
            var Q76;
            Q76=makeQuery(id+"F5.boolean.opBoolean","COPY",EDGE,{"derivedFrom":makeQuery(id+"F5.opExtrude","SWEPT_EDGE",EDGE,{"disambiguationData":[OSD([sQuery(id+"F4.wireOp",EDGE,"E49.top"),sQuery(id+"F4.wireOp",EDGE,"E49.left")])]})});
            var Q77;
            Q77=makeQuery(id+"F5.boolean.opBoolean","COPY",EDGE,{"derivedFrom":makeQuery(id+"F5.opExtrude","SWEPT_EDGE",EDGE,{"disambiguationData":[OSD([sQuery(id+"F4.wireOp",EDGE,"E48.top"),sQuery(id+"F4.wireOp",EDGE,"E48.left")])]})});
            var Q78;
            Q78=makeQuery(id+"F5.boolean.opBoolean","COPY",EDGE,{"derivedFrom":makeQuery(id+"F5.opExtrude","SWEPT_EDGE",EDGE,{"disambiguationData":[OSD([sQuery(id+"F4.wireOp",EDGE,"E34.top"),sQuery(id+"F4.wireOp",EDGE,"E34.left")])]})});
            var Q79;
            Q79=makeQuery(id+"F5.boolean.opBoolean","COPY",EDGE,{"derivedFrom":makeQuery(id+"F5.opExtrude","SWEPT_EDGE",EDGE,{"disambiguationData":[OSD([sQuery(id+"F4.wireOp",EDGE,"E35.top"),sQuery(id+"F4.wireOp",EDGE,"E35.left")])]})});
            var Q80;
            Q80=makeQuery(id+"F5.boolean.opBoolean","COPY",EDGE,{"derivedFrom":makeQuery(id+"F5.opExtrude","SWEPT_EDGE",EDGE,{"disambiguationData":[OSD([sQuery(id+"F4.wireOp",EDGE,"E36.top"),sQuery(id+"F4.wireOp",EDGE,"E36.left")])]})});
            var Q81;
            Q81=makeQuery(id+"F5.boolean.opBoolean","COPY",EDGE,{"derivedFrom":makeQuery(id+"F5.opExtrude","SWEPT_EDGE",EDGE,{"disambiguationData":[OSD([sQuery(id+"F4.wireOp",EDGE,"E37.top"),sQuery(id+"F4.wireOp",EDGE,"E37.left")])]})});
            var Q82;
            Q82=makeQuery(id+"F5.boolean.opBoolean","COPY",EDGE,{"derivedFrom":makeQuery(id+"F5.opExtrude","SWEPT_EDGE",EDGE,{"disambiguationData":[OSD([sQuery(id+"F4.wireOp",EDGE,"E38.top"),sQuery(id+"F4.wireOp",EDGE,"E38.left")])]})});
            var Q83;
            Q83=makeQuery(id+"F5.boolean.opBoolean","COPY",EDGE,{"derivedFrom":makeQuery(id+"F5.opExtrude","SWEPT_EDGE",EDGE,{"disambiguationData":[OSD([sQuery(id+"F4.wireOp",EDGE,"E39.top"),sQuery(id+"F4.wireOp",EDGE,"E39.left")])]})});
            var Q84;
            Q84=makeQuery(id+"F5.boolean.opBoolean","COPY",EDGE,{"derivedFrom":makeQuery(id+"F5.opExtrude","SWEPT_EDGE",EDGE,{"disambiguationData":[OSD([sQuery(id+"F4.wireOp",EDGE,"E40.top"),sQuery(id+"F4.wireOp",EDGE,"E40.left")])]})});
            var Q85;
            Q85=makeQuery(id+"F5.boolean.opBoolean","COPY",EDGE,{"derivedFrom":makeQuery(id+"F5.opExtrude","SWEPT_EDGE",EDGE,{"disambiguationData":[OSD([sQuery(id+"F4.wireOp",EDGE,"E41.top"),sQuery(id+"F4.wireOp",EDGE,"E41.left")])]})});
            var Q86;
            Q86=makeQuery(id+"F5.boolean.opBoolean","COPY",EDGE,{"derivedFrom":makeQuery(id+"F5.opExtrude","SWEPT_EDGE",EDGE,{"disambiguationData":[OSD([sQuery(id+"F4.wireOp",EDGE,"E53.top"),sQuery(id+"F4.wireOp",EDGE,"E53.left")])]})});
            var Q87;
            Q87=makeQuery(id+"F5.boolean.opBoolean","COPY",EDGE,{"derivedFrom":makeQuery(id+"F5.opExtrude","SWEPT_EDGE",EDGE,{"disambiguationData":[OSD([sQuery(id+"F4.wireOp",EDGE,"E52.top"),sQuery(id+"F4.wireOp",EDGE,"E52.left")])]})});
            var Q88;
            Q88=makeQuery(id+"F5.boolean.opBoolean","COPY",EDGE,{"derivedFrom":makeQuery(id+"F5.opExtrude","SWEPT_EDGE",EDGE,{"disambiguationData":[OSD([sQuery(id+"F4.wireOp",EDGE,"E47.top"),sQuery(id+"F4.wireOp",EDGE,"E47.left")])]})});
            var Q89;
            Q89=makeQuery(id+"F5.boolean.opBoolean","COPY",EDGE,{"derivedFrom":makeQuery(id+"F5.opExtrude","SWEPT_EDGE",EDGE,{"disambiguationData":[OSD([sQuery(id+"F4.wireOp",EDGE,"E33.top"),sQuery(id+"F4.wireOp",EDGE,"E33.left")])]})});
            var Q90;
            Q90=makeQuery(id+"F5.boolean.opBoolean","COPY",EDGE,{"derivedFrom":makeQuery(id+"F5.opExtrude","SWEPT_EDGE",EDGE,{"disambiguationData":[OSD([sQuery(id+"F4.wireOp",EDGE,"E41.top"),sQuery(id+"F4.wireOp",EDGE,"E41.right")])]})});
            var Q91;
            Q91=makeQuery(id+"F5.boolean.opBoolean","COPY",EDGE,{"derivedFrom":makeQuery(id+"F5.opExtrude","SWEPT_EDGE",EDGE,{"disambiguationData":[OSD([sQuery(id+"F4.wireOp",EDGE,"E40.top"),sQuery(id+"F4.wireOp",EDGE,"E40.right")])]})});
            var Q92;
            Q92=makeQuery(id+"F5.boolean.opBoolean","COPY",EDGE,{"derivedFrom":makeQuery(id+"F5.opExtrude","SWEPT_EDGE",EDGE,{"disambiguationData":[OSD([sQuery(id+"F4.wireOp",EDGE,"E39.top"),sQuery(id+"F4.wireOp",EDGE,"E39.right")])]})});
            var Q93;
            Q93=makeQuery(id+"F5.boolean.opBoolean","COPY",EDGE,{"derivedFrom":makeQuery(id+"F5.opExtrude","SWEPT_EDGE",EDGE,{"disambiguationData":[OSD([sQuery(id+"F4.wireOp",EDGE,"E38.top"),sQuery(id+"F4.wireOp",EDGE,"E38.right")])]})});
            var Q94;
            Q94=makeQuery(id+"F5.boolean.opBoolean","COPY",EDGE,{"derivedFrom":makeQuery(id+"F5.opExtrude","SWEPT_EDGE",EDGE,{"disambiguationData":[OSD([sQuery(id+"F4.wireOp",EDGE,"E37.top"),sQuery(id+"F4.wireOp",EDGE,"E37.right")])]})});
            var Q95;
            Q95=makeQuery(id+"F5.boolean.opBoolean","COPY",EDGE,{"derivedFrom":makeQuery(id+"F5.opExtrude","SWEPT_EDGE",EDGE,{"disambiguationData":[OSD([sQuery(id+"F4.wireOp",EDGE,"E36.top"),sQuery(id+"F4.wireOp",EDGE,"E36.right")])]})});
            var Q96;
            Q96=makeQuery(id+"F5.boolean.opBoolean","COPY",EDGE,{"derivedFrom":makeQuery(id+"F5.opExtrude","SWEPT_EDGE",EDGE,{"disambiguationData":[OSD([sQuery(id+"F4.wireOp",EDGE,"E35.top"),sQuery(id+"F4.wireOp",EDGE,"E35.right")])]})});
            var Q97;
            Q97=makeQuery(id+"F5.boolean.opBoolean","COPY",EDGE,{"derivedFrom":makeQuery(id+"F5.opExtrude","SWEPT_EDGE",EDGE,{"disambiguationData":[OSD([sQuery(id+"F4.wireOp",EDGE,"E51.top"),sQuery(id+"F4.wireOp",EDGE,"E51.right")])]})});
            var Q98;
            Q98=makeQuery(id+"F5.boolean.opBoolean","COPY",EDGE,{"derivedFrom":makeQuery(id+"F5.opExtrude","SWEPT_EDGE",EDGE,{"disambiguationData":[OSD([sQuery(id+"F4.wireOp",EDGE,"E46.top"),sQuery(id+"F4.wireOp",EDGE,"E46.right")])]})});
            var Q99;
            Q99=makeQuery(id+"F5.boolean.opBoolean","COPY",EDGE,{"derivedFrom":makeQuery(id+"F5.opExtrude","SWEPT_EDGE",EDGE,{"disambiguationData":[OSD([sQuery(id+"F4.wireOp",EDGE,"E45.top"),sQuery(id+"F4.wireOp",EDGE,"E45.right")])]})});
            var Q100;
            Q100=makeQuery(id+"F5.boolean.opBoolean","COPY",EDGE,{"derivedFrom":makeQuery(id+"F5.opExtrude","SWEPT_EDGE",EDGE,{"disambiguationData":[OSD([sQuery(id+"F4.wireOp",EDGE,"E44.top"),sQuery(id+"F4.wireOp",EDGE,"E44.right")])]})});
            var Q101;
            Q101=makeQuery(id+"F5.boolean.opBoolean","COPY",EDGE,{"derivedFrom":makeQuery(id+"F5.opExtrude","SWEPT_EDGE",EDGE,{"disambiguationData":[OSD([sQuery(id+"F4.wireOp",EDGE,"E43.top"),sQuery(id+"F4.wireOp",EDGE,"E43.right")])]})});
            var Q102;
            Q102=makeQuery(id+"F5.boolean.opBoolean","COPY",EDGE,{"derivedFrom":makeQuery(id+"F5.opExtrude","SWEPT_EDGE",EDGE,{"disambiguationData":[OSD([sQuery(id+"F4.wireOp",EDGE,"E42.top"),sQuery(id+"F4.wireOp",EDGE,"E42.right")])]})});
            var Q103;
            Q103=makeQuery(id+"F5.boolean.opBoolean","COPY",EDGE,{"derivedFrom":makeQuery(id+"F5.opExtrude","SWEPT_EDGE",EDGE,{"disambiguationData":[OSD([sQuery(id+"F4.wireOp",EDGE,"E59.top"),sQuery(id+"F4.wireOp",EDGE,"E59.right")])]})});
            var Q104;
            Q104=makeQuery(id+"F5.boolean.opBoolean","COPY",EDGE,{"derivedFrom":makeQuery(id+"F5.opExtrude","SWEPT_EDGE",EDGE,{"disambiguationData":[OSD([sQuery(id+"F4.wireOp",EDGE,"E58.top"),sQuery(id+"F4.wireOp",EDGE,"E58.right")])]})});
            var Q105;
            Q105=makeQuery(id+"F5.boolean.opBoolean","COPY",EDGE,{"derivedFrom":makeQuery(id+"F5.opExtrude","SWEPT_EDGE",EDGE,{"disambiguationData":[OSD([sQuery(id+"F4.wireOp",EDGE,"E61.top"),sQuery(id+"F4.wireOp",EDGE,"E61.right")])]})});
            var Q106;
            Q106=makeQuery(id+"F5.boolean.opBoolean","COPY",EDGE,{"derivedFrom":makeQuery(id+"F5.opExtrude","SWEPT_EDGE",EDGE,{"disambiguationData":[OSD([sQuery(id+"F4.wireOp",EDGE,"E60.top"),sQuery(id+"F4.wireOp",EDGE,"E60.right")])]})});
            var Q107;
            Q107=makeQuery(id+"F5.boolean.opBoolean","COPY",EDGE,{"derivedFrom":makeQuery(id+"F5.opExtrude","SWEPT_EDGE",EDGE,{"disambiguationData":[OSD([sQuery(id+"F4.wireOp",EDGE,"E57.top"),sQuery(id+"F4.wireOp",EDGE,"E57.right")])]})});
            var Q108;
            Q108=makeQuery(id+"F5.boolean.opBoolean","COPY",EDGE,{"derivedFrom":makeQuery(id+"F5.opExtrude","SWEPT_EDGE",EDGE,{"disambiguationData":[OSD([sQuery(id+"F4.wireOp",EDGE,"E56.top"),sQuery(id+"F4.wireOp",EDGE,"E56.right")])]})});
            var Q109;
            Q109=makeQuery(id+"F5.boolean.opBoolean","COPY",EDGE,{"derivedFrom":makeQuery(id+"F5.opExtrude","SWEPT_EDGE",EDGE,{"disambiguationData":[OSD([sQuery(id+"F4.wireOp",EDGE,"E34.top"),sQuery(id+"F4.wireOp",EDGE,"E34.right")])]})});
            var Q110;
            Q110=makeQuery(id+"F5.boolean.opBoolean","COPY",EDGE,{"derivedFrom":makeQuery(id+"F5.opExtrude","SWEPT_EDGE",EDGE,{"disambiguationData":[OSD([sQuery(id+"F4.wireOp",EDGE,"E33.top"),sQuery(id+"F4.wireOp",EDGE,"E33.right")])]})});
            var Q111;
            Q111=makeQuery(id+"F5.boolean.opBoolean","COPY",EDGE,{"derivedFrom":makeQuery(id+"F5.opExtrude","SWEPT_EDGE",EDGE,{"disambiguationData":[OSD([sQuery(id+"F4.wireOp",EDGE,"E50.top"),sQuery(id+"F4.wireOp",EDGE,"E50.right")])]})});
            var Q112;
            Q112=makeQuery(id+"F5.boolean.opBoolean","COPY",EDGE,{"derivedFrom":makeQuery(id+"F5.opExtrude","SWEPT_EDGE",EDGE,{"disambiguationData":[OSD([sQuery(id+"F4.wireOp",EDGE,"E49.top"),sQuery(id+"F4.wireOp",EDGE,"E49.right")])]})});
            var Q113;
            Q113=makeQuery(id+"F5.boolean.opBoolean","COPY",EDGE,{"derivedFrom":makeQuery(id+"F5.opExtrude","SWEPT_EDGE",EDGE,{"disambiguationData":[OSD([sQuery(id+"F4.wireOp",EDGE,"E48.top"),sQuery(id+"F4.wireOp",EDGE,"E48.right")])]})});
            var Q114;
            Q114=makeQuery(id+"F5.boolean.opBoolean","COPY",EDGE,{"derivedFrom":makeQuery(id+"F5.opExtrude","SWEPT_EDGE",EDGE,{"disambiguationData":[OSD([sQuery(id+"F4.wireOp",EDGE,"E47.top"),sQuery(id+"F4.wireOp",EDGE,"E47.right")])]})});
            var Q115;
            Q115=makeQuery(id+"F5.boolean.opBoolean","COPY",EDGE,{"derivedFrom":makeQuery(id+"F5.opExtrude","SWEPT_EDGE",EDGE,{"disambiguationData":[OSD([sQuery(id+"F4.wireOp",EDGE,"E52.top"),sQuery(id+"F4.wireOp",EDGE,"E52.right")])]})});
            var Q116;
            Q116=makeQuery(id+"F5.boolean.opBoolean","COPY",EDGE,{"derivedFrom":makeQuery(id+"F5.opExtrude","SWEPT_EDGE",EDGE,{"disambiguationData":[OSD([sQuery(id+"F4.wireOp",EDGE,"E53.top"),sQuery(id+"F4.wireOp",EDGE,"E53.right")])]})});
            var Q117;
            Q117=makeQuery(id+"F5.boolean.opBoolean","COPY",EDGE,{"derivedFrom":makeQuery(id+"F5.opExtrude","SWEPT_EDGE",EDGE,{"disambiguationData":[OSD([sQuery(id+"F4.wireOp",EDGE,"E54.top"),sQuery(id+"F4.wireOp",EDGE,"E54.right")])]})});
            var Q118;
            Q118=makeQuery(id+"F5.boolean.opBoolean","COPY",EDGE,{"derivedFrom":makeQuery(id+"F5.opExtrude","SWEPT_EDGE",EDGE,{"disambiguationData":[OSD([sQuery(id+"F4.wireOp",EDGE,"E55.top"),sQuery(id+"F4.wireOp",EDGE,"E55.right")])]})});
            var Q119;
            Q119=makeQuery(id+"F5.boolean.opBoolean","COPY",EDGE,{"derivedFrom":makeQuery(id+"F5.opExtrude","SWEPT_EDGE",EDGE,{"disambiguationData":[OSD([sQuery(id+"F4.wireOp",EDGE,"E49.bottom"),sQuery(id+"F4.wireOp",EDGE,"E49.right")])]})});
            fillet(context, id + "F6", {"entities" : qUnion([Q0, Q1, Q2, Q3, Q4, Q5, Q6, Q7, Q8, Q9, Q10, Q11, Q12, Q13, Q14, Q15, Q16, Q17, Q18, Q19, Q20, Q21, Q22, Q23, Q24, Q25, Q26, Q27, Q28, Q29, Q30, Q31, Q32, Q33, Q34, Q35, Q36, Q37, Q38, Q39, Q40, Q41, Q42, Q43, Q44, Q45, Q46, Q47, Q48, Q49, Q50, Q51, Q52, Q53, Q54, Q55, Q56, Q57, Q58, Q59, Q60, Q61, Q62, Q63, Q64, Q65, Q66, Q67, Q68, Q69, Q70, Q71, Q72, Q73, Q74, Q75, Q76, Q77, Q78, Q79, Q80, Q81, Q82, Q83, Q84, Q85, Q86, Q87, Q88, Q89, Q90, Q91, Q92, Q93, Q94, Q95, Q96, Q97, Q98, Q99, Q100, Q101, Q102, Q103, Q104, Q105, Q106, Q107, Q108, Q109, Q110, Q111, Q112, Q113, Q114, Q115, Q116, Q117, Q118, Q119]), "radius" : 1.2 * mm, "tangentPropagation" : true, "allowEdgeOverflow" : false});
        }
    });
